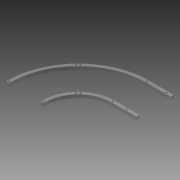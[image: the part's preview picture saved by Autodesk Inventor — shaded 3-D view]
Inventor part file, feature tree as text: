
AUTODESK INVENTOR PART (.ipt)
format: ipt  version: 2013 (Build 170138000, 138)  size: 118,784 bytes
history: native  units: in
note: dims shown in document units (in); Inventor stores cm internally (conversion verified against a paired STEP export)
features: extrude x1, sketch x1
ambient origin geometry x8: Origin, YZ Plane, XZ Plane, XY Plane, X Axis, Y Axis, Z Axis, Center Point
bodies: Solid1 (feature_tree)
feature tree (2):
  extrude  "Extrusion1"  Depth=0.5in TaperAngle=0.0deg
  sketch  "Sketch1"  dims[d2=0.5in d3=0.5in d10=0.5in d11=0.5in d13=0.5in d14=0.266in d15=0.266in d16=0.266in d18=0.266in d20=0.25in d21=0.266in d22=0.266in d23=0.266in d24=0.25in d26=0.266in d27=0.25in d30=0.266in d31=0.25in d32=0.266in d33=0.25in d34=0.5in d35=0.0in]
